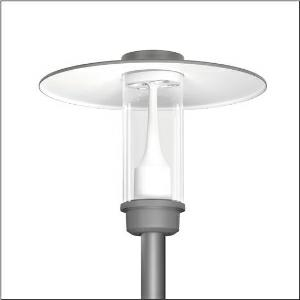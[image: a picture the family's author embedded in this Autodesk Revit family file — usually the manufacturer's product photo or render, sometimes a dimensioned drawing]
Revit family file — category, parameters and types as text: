
# Revit family: litepole_2_iq___pl1_2s_5xa5425of14h_0dca
name_source: partatom
category: Lighting Fixtures
units: mm (PartAtom-declared; Revit-internal decimal feet)

## family parameters
Cut with Voids When Loaded = No
Host = Face
Light Source = No
Part Type = Normal
Room Calculation Point = No
Round Connector Dimension = Use Diameter
Shared = No

## types (1)
- --- (1 x LED, 3000 lm, 21.8 W, 2700K)
    Apparent Load = 22 VA
    CIE Flux Codes = 22 60 92 98 100
    Color Rendering = 70
    Color Temperature = 2700K
    Default Elevation = 1800 mm
    Description = Litepole 2 iQ, mast luminaire, Module 540 iQ-SR, primary light control with 3 zone facetted reflector, of plastic, silver coated, highly specular, structured, primary optical cover: cover, of PMMA, transparent, light distribution: PL1.2s, light emission: direct distribution, primary light characteristic: symmetric, installation type: post-top, LED, High Power LED, rated luminous flux: 2.990lm, luminous efficacy: 137lm/W, light colour: 727, colour temperature: 2700K, control gear: iQ Street-Remote, control: pre-setting: logarithmic dimming characteristic, Street-Remote, Auto-Match, Temp-Guard, Lumen-Switch, Night-Set, Smart-Wire, Light-Fading, Desk-Remote (wireless, voltage-free reading and setting of iQ features in the workshop via application-optimized NFC function/RFID function), optimised constant luminous flux control (CLO 2.0), with terminal, 6-pole, max. 2.5mm², mains connection: 230..240V, AC, 50/60Hz, start of lifetime: 22W, end of service life: 23W, reduction: 11W, luminaire housing, upper part, of aluminium, coated, Siteco® metallic grey (DB 702S), diameter: 750mm, height: 590mm, spigot size: d x l = 76 x 70mm (post-top) | with reducer (optional accessory) 60 x 70mm, mounting height: 3..5m, post-top mast mounting element, of diecast aluminium, coated, Siteco® metallic grey (DB 702S), Module 540 iQ-SR, traffic white (RAL 9016), equipment: standard, protection rating (complete): IP65, insulation class (complete): insulation class II (safety insulation), certification: CE, ENEC, VDE, packaging unit: 1 piece

Light Distribution: PL1.2s
    Height = 590 mm
    Lamp = 1 x LED
    Lamp Light Flux = 3000 lm
    Lamp Power = 21.8 W
    Lamp count = 1
    Length = 750 mm
    Luminous efficacy = 138 lm/W
    Manufacturer = Siteco
    ModVariant = No
    Model = 5XA5425OF14H
    Number of Poles = 1
    OnlyDefault = Yes
    Power Factor = 1
    Product Name = Litepole 2 iQ | PL1.2s
    Product group = mast luminaire | pylon top
    ProductGroupID = 6100
    Protection Class = Protection class II
    Protection Degree = IP 65
    RLX_Detail_Level = 1
    RLX_Emergency_Light_Flux = 0 lm
    RLX_Emergency_Type = 0
    RLX_Emergency_Type_DB = No
    RlxData = <blob elided: 29425 chars, md5=64b4473e>
    Socket = socket
    Standby Power = 0 W
    System Light Flux = 3000 lm
    System Power = 22 W
    Type Comments = factory setting: luminous flux: 100 % | dim-lin: 254 | 456 mA
    Type Image = l_1006518.jpg
    URL = http://relux.com
    VarID = @adj_144033
    Voltage = 0 V
    Weight = 0.00 kg
    Width = 0 mm  [stored 0 ft]

note: [stored X ft] marks values corroborated as IEEE doubles in the binary element streams (Revit-internal decimal feet)

## geometry (parser evidence)
native form markers: Blend x4, Sweep x9
no freeform markers — native parametric forms only
